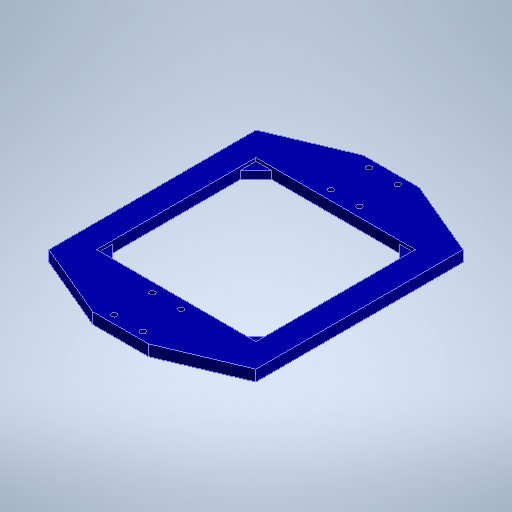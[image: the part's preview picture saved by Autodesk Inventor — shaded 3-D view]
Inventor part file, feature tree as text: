
AUTODESK INVENTOR PART (.ipt)
format: ipt  version: 2025.2 (Build 292293000, 293)  size: 311,808 bytes
history: native  units: mm
features: extrude x2, sketch x1, hole x1
ambient origin geometry x8: Origin, YZ Plane, XZ Plane, XY Plane, X Axis, Y Axis, Z Axis, Center Point
bodies: Solid1 (feature_tree)
feature tree (4):
  sketch  "Sketch1"  dims[d0=100.0mm d1=100.0mm d4=130.0mm d5=170.0mm d6=20.0mm d7=40.0mm d8=40.0mm d10=7.5mm d11=7.5mm d12=20.0mm d13=47.5mm d14=10.0mm d15=10.0mm d16=10.0mm d17=10.0mm d18=5.0mm d19=0.0mm d20=2.0mm d21=0.0mm d22=5.0mm d23=18.0mm d24=24.0mm d25=5.0mm d26=18.0mm d27=24.0mm d28=3.4mm d29=6.0mm d30=4.0mm d31=2.0mm d32=90.0deg d33=8.0mm d34=20.594885mm]
  extrude  "Extrusion1"  Depth=100.0mm
  extrude  "Extrusion2"  Depth=130.0mm
  hole  "Hole1"  [1 undecoded]
note: 1 required parameter value undecoded (feature->parameter linkage not recoverable at this tier; creation-order binding heuristic only, values carry confidence <= 0.55)
